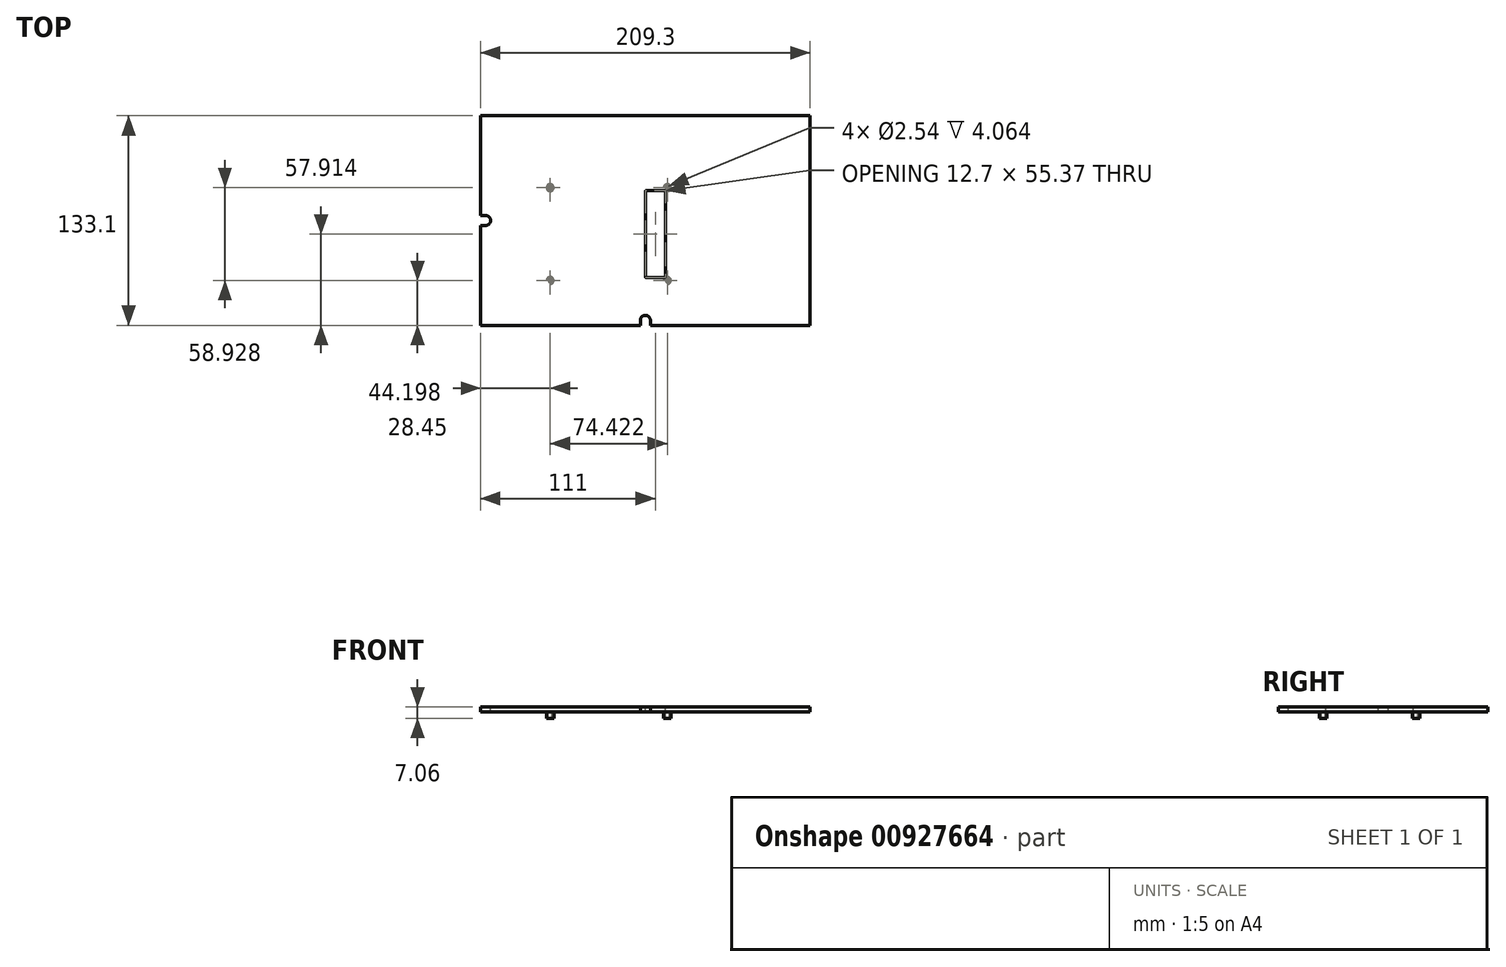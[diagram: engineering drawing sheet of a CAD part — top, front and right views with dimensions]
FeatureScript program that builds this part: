
annotation { "Feature Type Name" : "Feature", "Feature Type Description" : "" }
export const myFeature = defineFeature(function(context is Context, id is Id, definition is map)
    precondition{}
    {
        {
            var Q0;
            Q0=qCreatedBy(makeId("Top.planeOp"),FACE);
            var sketch = newSketch(context, id + "F0", { "sketchPlane" : qUnion([Q0])});
            skLineSegment(sketch, "E0.bottom", {"start": v(104.65, -66.55) * mm, "end": v(-104.65, -66.55) * mm});
            skLineSegment(sketch, "E0.top", {"start": v(104.65, 66.55) * mm, "end": v(-104.65, 66.55) * mm});
            skLineSegment(sketch, "E0.left", {"start": v(104.65, -66.55) * mm, "end": v(104.65, 66.55) * mm});
            skLineSegment(sketch, "E0.right", {"start": v(-104.65, -66.55) * mm, "end": v(-104.65, 66.55) * mm});
            skPoint(sketch, "E0.middle", {"position": v(0, 0) * mm});
            skSolve(sketch);
        }
        {
            var Q0;
            Q0=qSketchRegion(id+"F0",true);
            extrude(context, id + "F1", {"entities" : qUnion([Q0]), "depth" : 3 * mm, "offsetDistance" : 25.4 * mm});
        }
        {
            var Q0;
            Q0=makeQuery(id+"F1.opExtrude","CAP_FACE",FACE,{"disambiguationData":[OSD([sQuery(id+"F0.wireOp",EDGE,"E0.bottom"),sQuery(id+"F0.wireOp",EDGE,"E0.top"),sQuery(id+"F0.wireOp",EDGE,"E0.left"),sQuery(id+"F0.wireOp",EDGE,"E0.right")])],"isStart":false});
            var sketch = newSketch(context, id + "F2", { "sketchPlane" : qUnion([Q0])});
            skLineSegment(sketch, "E1.bottom", {"start": v(0, 19.05) * mm, "end": v(12.7, 19.05) * mm});
            skLineSegment(sketch, "E1.top", {"start": v(0, -36.32) * mm, "end": v(12.7, -36.32) * mm});
            skLineSegment(sketch, "E1.left", {"start": v(0, 19.05) * mm, "end": v(0, -36.32) * mm});
            skLineSegment(sketch, "E1.right", {"start": v(12.7, 19.05) * mm, "end": v(12.7, -36.32) * mm});
            skArc(sketch, "E2", {"start": v(-3.18, -63.37) * mm, "mid": v(0, -60.2) * mm, "end": v(3.18, -63.37) * mm});
            skLineSegment(sketch, "E3", {"start": v(-3.18, -66.55) * mm, "end": v(3.18, -66.55) * mm});
            skLineSegment(sketch, "E4", {"start": v(-3.18, -66.55) * mm, "end": v(-3.18, -63.37) * mm});
            skLineSegment(sketch, "E5", {"start": v(3.17, -63.37) * mm, "end": v(3.17, -66.55) * mm});
            skLineSegment(sketch, "E6", {"start": v(-104.65, 3.17) * mm, "end": v(-104.65, -3.18) * mm});
            skPoint(sketch, "E7", {"position": v(-104.65, 0) * mm});
            skLineSegment(sketch, "E8", {"start": v(-104.65, -3.18) * mm, "end": v(-101.47, -3.18) * mm});
            skLineSegment(sketch, "E9", {"start": v(-104.65, 3.17) * mm, "end": v(-101.47, 3.17) * mm});
            skArc(sketch, "E10", {"start": v(-101.47, -3.17) * mm, "mid": v(-98.3, 0) * mm, "end": v(-101.47, 3.17) * mm});
            skSolve(sketch);
        }
        {
            var Q0;
            Q0=qSketchRegion(id+"F2",true);
            extrude(context, id + "F3", {"entities" : qUnion([Q0]), "operationType" : NewBodyOperationType.REMOVE, "endBound" : BoundingType.THROUGH_ALL, "oppositeDirection" : true, "depth" : 25.4 * mm, "offsetDistance" : 25.4 * mm});
        }
        {
            var Q0;
            Q0=makeQuery(id+"F1.opExtrude","CAP_FACE",FACE,{"disambiguationData":[OSD([sQuery(id+"F0.wireOp",EDGE,"E0.bottom"),sQuery(id+"F0.wireOp",EDGE,"E0.top"),sQuery(id+"F0.wireOp",EDGE,"E0.left"),sQuery(id+"F0.wireOp",EDGE,"E0.right")])],"isStart":true});
            var sketch = newSketch(context, id + "F4", { "sketchPlane" : qUnion([Q0])});
            skCircle(sketch, "E11", {"center": v(-60.45, 38.1) * mm, "radius": 1.27 * mm});
            skCircle(sketch, "E12", {"center": v(13.97, 38.1) * mm, "radius": 1.27 * mm});
            skCircle(sketch, "E13", {"center": v(-60.45, -20.83) * mm, "radius": 1.27 * mm});
            skCircle(sketch, "E14", {"center": v(13.97, -20.83) * mm, "radius": 1.27 * mm});
            skCircle(sketch, "E15", {"center": v(-60.45, 38.1) * mm, "radius": 2.39 * mm});
            skCircle(sketch, "E16", {"center": v(13.97, 38.1) * mm, "radius": 2.39 * mm});
            skCircle(sketch, "E17", {"center": v(13.97, -20.83) * mm, "radius": 2.39 * mm});
            skCircle(sketch, "E18", {"center": v(-60.45, -20.83) * mm, "radius": 2.39 * mm});
            skLineSegment(sketch, "E19", {"start": v(13.97, 38.1) * mm, "end": v(13.97, -20.83) * mm, "construction": true});
            skPoint(sketch, "E20", {"position": v(0, 8.64) * mm});
            skPoint(sketch, "E21", {"position": v(13.97, 8.64) * mm});
            skPoint(sketch, "E22", {"position": v(6.35, 36.32) * mm});
            skSolve(sketch);
        }
        {
            var Q0;
            Q0 = qSketchRegion(id + "F4", true);
            extrude(context, id + "F5", {"entities" : qUnion([Q0]), "operationType" : NewBodyOperationType.ADD, "depth" : 4.06 * mm, "offsetDistance" : 25.4 * mm});
        }
        {
            var Q0;
            Q0=makeQuery(id+"F3.boolean.opBoolean","COPY",EDGE,{"derivedFrom":makeQuery(id+"F3.opExtrude","SWEPT_EDGE",EDGE,{"disambiguationData":[OSD([sQuery(id+"F2.wireOp",EDGE,"E1.top"),sQuery(id+"F2.wireOp",EDGE,"E1.right")])]})});
            var Q1;
            Q1=makeQuery(id+"F3.boolean.opBoolean","COPY",EDGE,{"derivedFrom":makeQuery(id+"F3.opExtrude","SWEPT_EDGE",EDGE,{"disambiguationData":[OSD([sQuery(id+"F2.wireOp",EDGE,"E1.top"),sQuery(id+"F2.wireOp",EDGE,"E1.left")])]})});
            var Q2;
            Q2=makeQuery(id+"F3.boolean.opBoolean","COPY",EDGE,{"derivedFrom":makeQuery(id+"F3.opExtrude","SWEPT_EDGE",EDGE,{"disambiguationData":[OSD([sQuery(id+"F2.wireOp",EDGE,"E1.bottom"),sQuery(id+"F2.wireOp",EDGE,"E1.left")])]})});
            var Q3;
            Q3=makeQuery(id+"F3.boolean.opBoolean","COPY",EDGE,{"derivedFrom":makeQuery(id+"F3.opExtrude","SWEPT_EDGE",EDGE,{"disambiguationData":[OSD([sQuery(id+"F2.wireOp",EDGE,"E1.bottom"),sQuery(id+"F2.wireOp",EDGE,"E1.right")])]})});
            fillet(context, id + "F6", {"entities" : qUnion([Q0, Q1, Q2, Q3]), "radius" : 0.5 * mm, "tangentPropagation" : true, "allowEdgeOverflow" : false});
        }
    });
